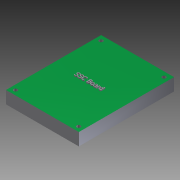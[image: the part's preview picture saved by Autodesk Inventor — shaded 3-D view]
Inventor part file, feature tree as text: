
AUTODESK INVENTOR PART (.ipt)
format: ipt  version: 2012 (Build 160160000, 160)  size: 390,144 bytes
history: native  units: mm
features: sketch x2, extrude x1, hole x1, emboss x1
ambient origin geometry x8: Origin, YZ Plane, XZ Plane, XY Plane, X Axis, Y Axis, Z Axis, Center Point
bodies: Solid1 (feature_tree)
feature tree (5):
  extrude  "Extrusion1"  Depth=10.0mm TaperAngle=0.0deg
  sketch  "Sketch2"  dims[d11=3.0mm d12=3.0mm d13=3.0mm d14=58.44mm d15=76.3mm d16=50.55mm d17=68.5mm d18=68.5mm d19=50.55mm d20=3.0mm d21=6.0mm d22=4.0mm d23=2.0mm d24=90.0deg d25=8.0mm d26=20.594885mm d27=1.0mm d28=0.0mm]
  hole  "Hole1"  [1 undecoded]
  emboss  "Emboss1"
  sketch  "Sketch1"  dims[d0=3.0mm d1=3.0mm d2=3.0mm d3=58.44mm d4=76.3mm d5=50.55mm d6=68.5mm d7=68.5mm d8=50.55mm d9=10.0mm d10=0.0mm]
note: 1 required parameter value undecoded (feature->parameter linkage not recoverable at this tier; creation-order binding heuristic only, values carry confidence <= 0.55)
